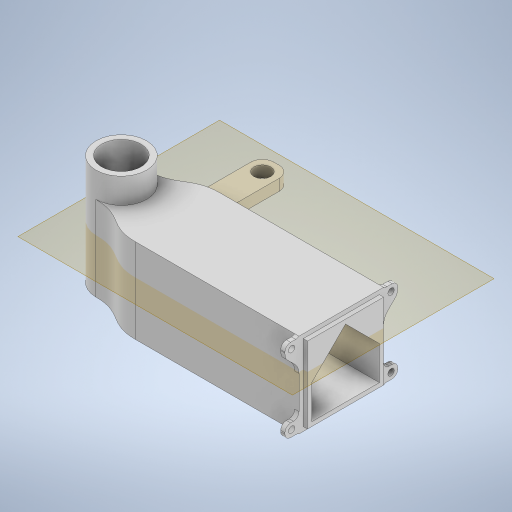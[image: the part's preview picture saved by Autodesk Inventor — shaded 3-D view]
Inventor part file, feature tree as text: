
AUTODESK INVENTOR PART (.ipt)
format: ipt  version: 2024 (Build 280153000, 153)  size: 520,192 bytes
history: native  units: in
note: dims shown in document units (in); Inventor stores cm internally (conversion verified against a paired STEP export)
features: extrude x8, sketch x7, fillet x4, projected_geometry x3, plane x2, hole x1, chamfer x1
ambient origin geometry x8: Origin, YZ Plane, XZ Plane, XY Plane, X Axis, Y Axis, Z Axis, Center Point
bodies: Solid1 (feature_tree)
feature tree (26):
  extrude  "Extrusion1"  Depth=0.0787in
  plane  "Work Plane1"
  extrude  "Extrusion2"  Depth=0.374in
  sketch  "Sketch4"  dims[d5=1.1811in d6=0.1181in]
  extrude  "Extrusion4"  Depth=0.1181in
  hole  "Hole2"  [1 undecoded]
  sketch  "Sketch9"  dims[d10=0.4724in d11=0.1181in]
  extrude  "Extrusion7"  Depth=0.1181in
  extrude  "Extrusion8"  Depth=1.1811in
  extrude  "Extrusion9"  Depth=0.1575in TaperAngle=0.0deg
  extrude  "Extrusion3"  Depth=0.1575in
  fillet  "Fillet1"  Radius=1.1811in
  chamfer  "Chamfer1"  Distance=1.1811in
  fillet  "Fillet2"  Radius=0.0591in
  plane  "Work Plane3"
  extrude  "Extrusion10"  Depth=0.1575in TaperAngle=0.0deg
  fillet  "Fillet3"  Radius=0.0591in
  fillet  "Fillet4"  Radius=0.748in
  sketch  "Sketch1"  dims[d0=0.7087in d1=0.0787in]
  sketch  "Sketch2"  dims[d2=0.4724in d3=0.0in d4=0.374in]
  projected_geometry  "Projected Loop1"
  sketch  "Sketch8"  dims[d7=0.1181in d9=0.9449in]
  projected_geometry  "Projected Loop5"
  sketch  "Sketch11"  dims[d12=0.1181in d13=1.1811in]
  sketch  "Sketch12"  dims[d20=0.1181in d23=2.7559in d24=0.0in d25=0.0886in d26=1.1811in d27=1.1811in d35=0.0591in d36=0.2362in d37=0.0in d38=0.0591in d39=0.0in d40=0.748in d41=0.0in d53=0.5906in d54=0.1033in d55=0.1033in d56=0.1033in d57=0.1033in d58=0.1033in d60=0.1033in d61=0.1033in d62=0.5906in d63=0.2362in d64=0.1575in d65=0.0787in d66=90.0deg d67=0.3937in d68=0.8108in d69=0.7874in d70=0.0787in d71=0.0787in d72=0.0in d73=0.0in d74=1.1811in d75=0.0in d76=0.1033in d77=0.1033in d78=0.1033in d79=0.1033in d80=0.1772in d82=0.1772in d86=0.0591in d87=0.0in d91=0.0787in d92=0.0148in d93=0.0886in d94=0.1969in d95=0.1969in d99=0.0148in d100=0.1772in d101=0.0787in d102=45.0deg d103=0.1969in d104=0.4724in d105=0.4724in d106=0.4724in d107=0.2362in d108=0.3937in d109=1.5748in d110=0.3937in d111=0.1969in d113=0.1969in d114=0.1575in d115=0.0in d116=0.1969in d117=0.1575in d119=-0.315in]
  projected_geometry  "Projected Loop6"
note: 1 required parameter value undecoded (feature->parameter linkage not recoverable at this tier; creation-order binding heuristic only, values carry confidence <= 0.55)
